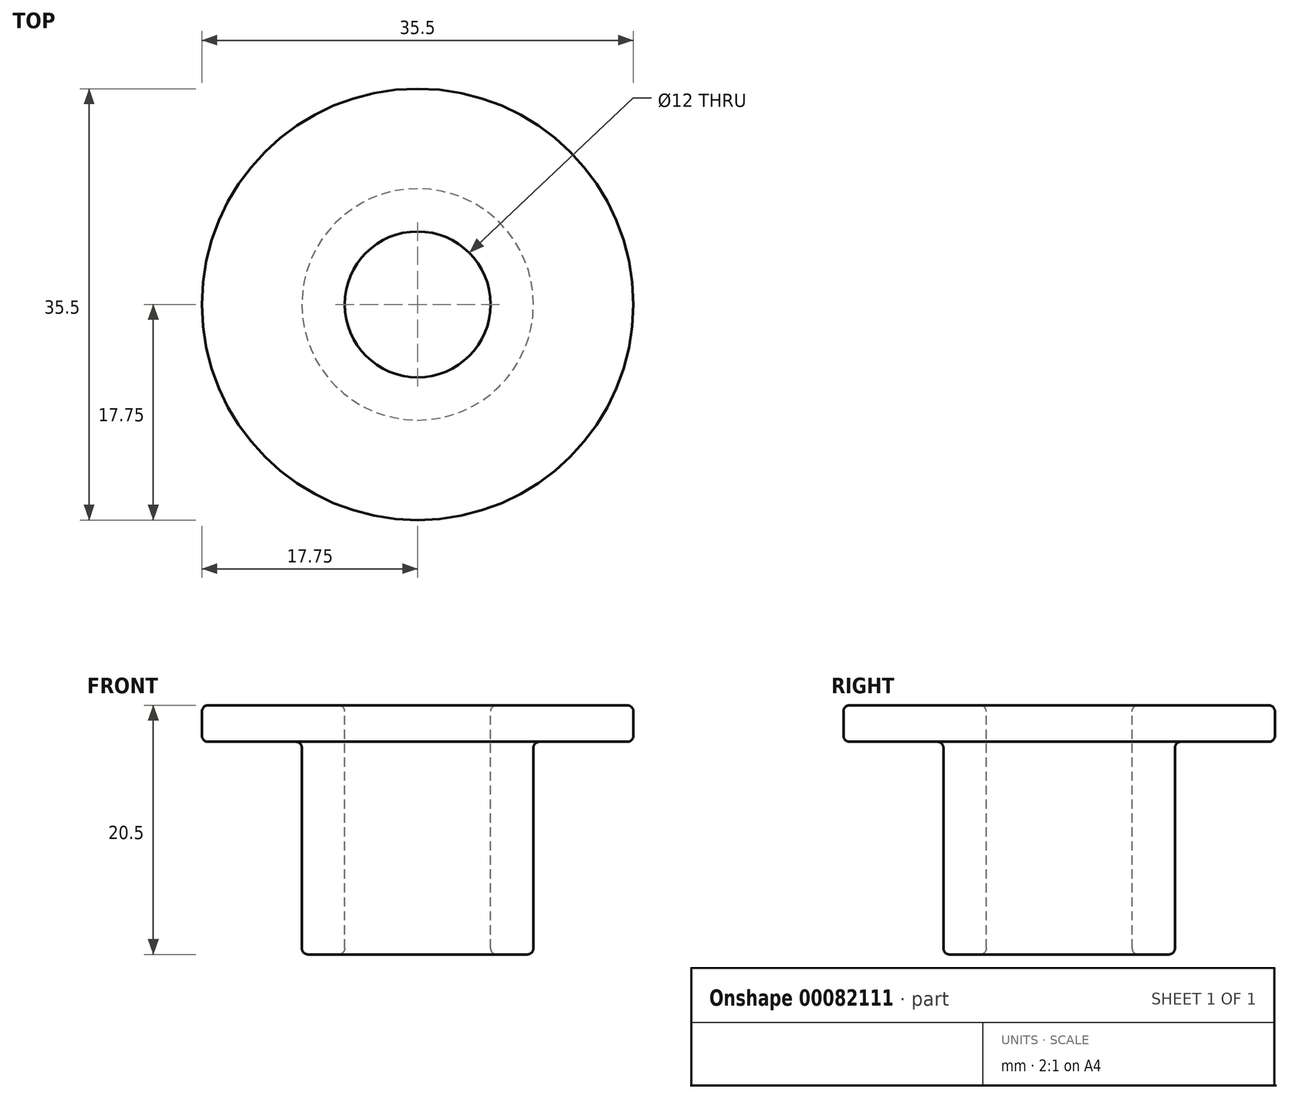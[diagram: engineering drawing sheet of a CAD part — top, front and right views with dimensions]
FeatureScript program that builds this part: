
annotation { "Feature Type Name" : "Feature", "Feature Type Description" : "" }
export const myFeature = defineFeature(function(context is Context, id is Id, definition is map)
    precondition{}
    {
        {
            var Q0;
            Q0=qCreatedBy(makeId("Top.planeOp"),FACE);
            var sketch = newSketch(context, id + "F0", { "sketchPlane" : qUnion([Q0])});
            skCircle(sketch, "E0", {"center": v(0, 0) * mm, "radius": 9.53 * mm});
            skCircle(sketch, "E1", {"center": v(0, 0) * mm, "radius": 6 * mm});
            skSolve(sketch);
        }
        {
            var Q0;
            Q0=qSketchRegion(id+"F0",true);
            extrude(context, id + "F1", {"entities" : qUnion([Q0]), "oppositeDirection" : true, "depth" : 17.5 * mm});
        }
        {
            var Q0;
            Q0=qCreatedBy(makeId("Top.planeOp"),FACE);
            var sketch = newSketch(context, id + "F2", { "sketchPlane" : qUnion([Q0])});
            skCircle(sketch, "E2", {"center": v(0, 0) * mm, "radius": 17.75 * mm});
            skCircle(sketch, "E3.0", {"center": v(0, 0) * mm, "radius": 6 * mm});
            skSolve(sketch);
        }
        {
            var Q0;
            Q0=qSketchRegion(id+"F2",true);
            extrude(context, id + "F3", {"entities" : qUnion([Q0]), "operationType" : NewBodyOperationType.ADD, "depth" : 3 * mm});
        }
        {
            var Q0;
            Q0=makeQuery(id+"F1.opExtrude","CAP_FACE",FACE,{"disambiguationData":[OSD([sQuery(id+"F0.wireOp",EDGE,"E0"),sQuery(id+"F0.wireOp",EDGE,"E1")])],"isStart":false});
            var Q1;
            Q1=makeQuery(id+"F3.opExtrude","CAP_FACE",FACE,{"disambiguationData":[OSD([sQuery(id+"F2.wireOp",EDGE,"E2"),sQuery(id+"F2.wireOp",EDGE,"E3.0")])],"isStart":true});
            var Q2;
            Q2=makeQuery(id+"F3.opExtrude","CAP_FACE",FACE,{"disambiguationData":[OSD([sQuery(id+"F2.wireOp",EDGE,"E2"),sQuery(id+"F2.wireOp",EDGE,"E3.0")])],"isStart":false});
            var Q3;
            Q3=makeQuery(id+"F4lnB6d4ua1G4HV_1.opExtrude","CAP_FACE",FACE,{"disambiguationData":[OSD([sQuery(id+"F1o2VQ54uIw4Ex2_1.wireOp",EDGE,"014a16ee-20fc-48ff-8fa4-6fc64fe1b2bb.0"),sQuery(id+"F1o2VQ54uIw4Ex2_1.wireOp",EDGE,"ljHVKjoa-xzqY-uHut-6uKP-OWjSY1WK4QRY")])],"isStart":false});
            fillet(context, id + "F4", {"entities" : qUnion([Q0, Q1, Q2, Q3]), "radius" : 0.5 * mm, "tangentPropagation" : true, "allowEdgeOverflow" : false});
        }
    });
